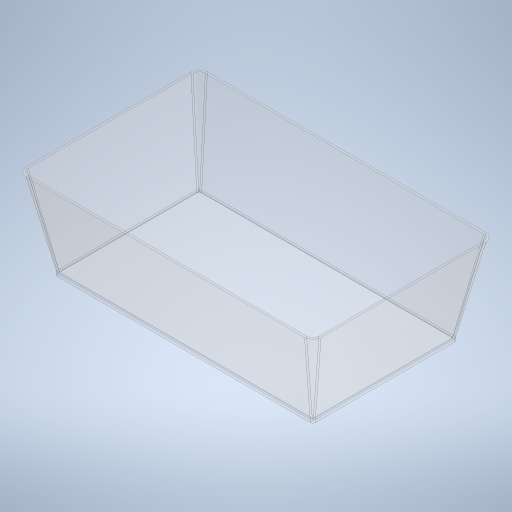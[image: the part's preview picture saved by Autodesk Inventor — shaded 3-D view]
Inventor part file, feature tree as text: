
AUTODESK INVENTOR PART (.ipt)
format: ipt  version: 2024 (Build 280153000, 153)  size: 406,016 bytes
history: native  units: in
note: dims shown in document units (in); Inventor stores cm internally (conversion verified against a paired STEP export)
features: sketch x5, extrude x4, projected_geometry x2, other x2, plane x1, fillet x1, loft x1, delete_face x1, thicken_offset x1
ambient origin geometry x8: Origin, YZ Plane, XZ Plane, XY Plane, X Axis, Y Axis, Z Axis, Center Point
bodies: Solid1 (feature_tree)
feature tree (18):
  extrude  "Extrusion1"  Depth=7.0in
  plane  "Work Plane1"
  extrude  "Extrusion2"  Depth=4.7in
  fillet  "Fillet2"  Radius=0.125in
  loft  "Loft2"
  extrude  "Extrusion3"  TaperAngle=0.0deg  [1 undecoded]
  delete_face  "Delete Face1"
  thicken_offset  "Thicken1"
  extrude  "Extrusion4"  Depth=0.1in
  sketch  "Sketch5"  dims[d18=0.0in d19=0.0in d20=0.1in d21=1.0in d22=15.0in d23=0.0in d24=0.0in]
  sketch  "Sketch1"  dims[d0=12.5in d1=7.0in]
  sketch  "Sketch2"  dims[d2=0.125in d3=0.0in d4=4.7in d5=0.125in]
  projected_geometry  "Projected Loop1"
  other  "Edges3"
  other  "Edges4"
  sketch  "Sketch3"  dims[d6=0.5in d7=0.0in d13=0.4in]
  sketch  "Sketch4"  dims[d14=0.0in d15=90.0deg d16=0.0in d17=90.0deg]
  projected_geometry  "Projected Loop2"
note: 1 required parameter value undecoded (feature->parameter linkage not recoverable at this tier; creation-order binding heuristic only, values carry confidence <= 0.55)
